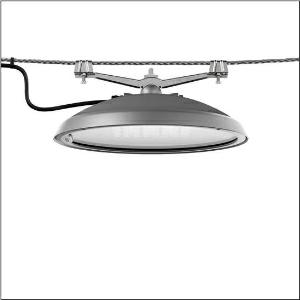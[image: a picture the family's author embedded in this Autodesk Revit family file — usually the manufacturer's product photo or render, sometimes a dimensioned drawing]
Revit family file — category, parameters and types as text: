
# Revit family: dl_r__50_iq_mini___st0_8s_5xa248v31f08fe_ae35
name_source: partatom
category: Lighting Fixtures
units: mm (PartAtom-declared; Revit-internal decimal feet)

## family parameters
Cut with Voids When Loaded = No
Host = Face
Light Source = No
Part Type = Normal
Room Calculation Point = No
Round Connector Dimension = Use Diameter
Shared = No

## types (1)
- --- (1 x LED, 2700 lm, 16.3 W, 3000K)
    Apparent Load = 16 VA
    CIE Flux Codes = 38 75 97 100 100
    Color Rendering = 70
    Color Temperature = 3000K
    Default Elevation = 1800 mm
    Description = DL® 50 iQ mini, catenary luminaire, primary light control with lens, of PMMA, primary optical cover: cover, of toughened safety glass, transparent, light distribution: ST0.8s, light emission: direct distribution, primary light characteristic: symmetric, installation type: suspended mounting, LED, High Power LED, rated luminous flux: 2.700lm, luminous efficacy: 166lm/W, light colour: 730, colour temperature: 3000K, control: optimised constant luminous flux control (CLO 2.0), Desk-Remote (wireless, voltage-free reading and setting of iQ features in the workshop via application-optimized NFC function/RFID function), Light-Fading, Smart-Wire, Night-Set, Lumen-Switch, Temp-Guard, Auto-Match, Street-Remote, mains connection: 230..240V, AC, 50/60Hz, start of lifetime: 16W, end of service life: 17W, reduction: 8W, luminaire housing, of diecast aluminium, powder-coated, Siteco® metallic grey (DB 702S), diameter: 500mm, height: 115mm, protection rating (complete): IP66, insulation class (complete): insulation class II (safety insulation), certification: CE, ENEC, ENEC+, VDE, impact resistance: IK08, permissible operating ambient temperature for outdoor applications: -25..+40°C, standard-compliant lighting for roads and squares, packaging unit: 1 piece

Light Distribution: ST0.8s
    Height = 124 mm
    Lamp = 1 x LED
    Lamp Light Flux = 2700 lm
    Lamp Power = 16.3 W
    Lamp count = 1
    Length = 500 mm
    Luminous efficacy = 166 lm/W
    Manufacturer = Siteco
    ModVariant = No
    Model = 5XA248V31F08FE
    Number of Poles = 1
    OnlyDefault = Yes
    Power Factor = 1
    Product Name = DL® 50 iQ mini | ST0.8s
    Product group = catenary luminaire
    ProductGroupID = 6300
    Protection Class = Protection class II
    Protection Degree = IP 66
    RLX_Detail_Level = 1
    RLX_Emergency_Light_Flux = 0 lm
    RLX_Emergency_Type = 0
    RLX_Emergency_Type_DB = No
    RlxData = <blob elided: 123037 chars, md5=ba0ee619>
    Socket = socket
    Standby Power = 0 W
    System Light Flux = 2700 lm
    System Power = 16 W
    Type Comments = factory setting: luminous flux: 100 % | dim-lin: 254 | 333 mA
    Type Image = l_1242791.jpg
    URL = http://relux.com
    VarID = @adj_107769
    Voltage = 0 V
    Weight = 0.00 kg
    Width = 0 mm  [stored 0 ft]

note: [stored X ft] marks values corroborated as IEEE doubles in the binary element streams (Revit-internal decimal feet)

## geometry (parser evidence)
native form markers: Blend x4, Sweep x11
no freeform markers — native parametric forms only
